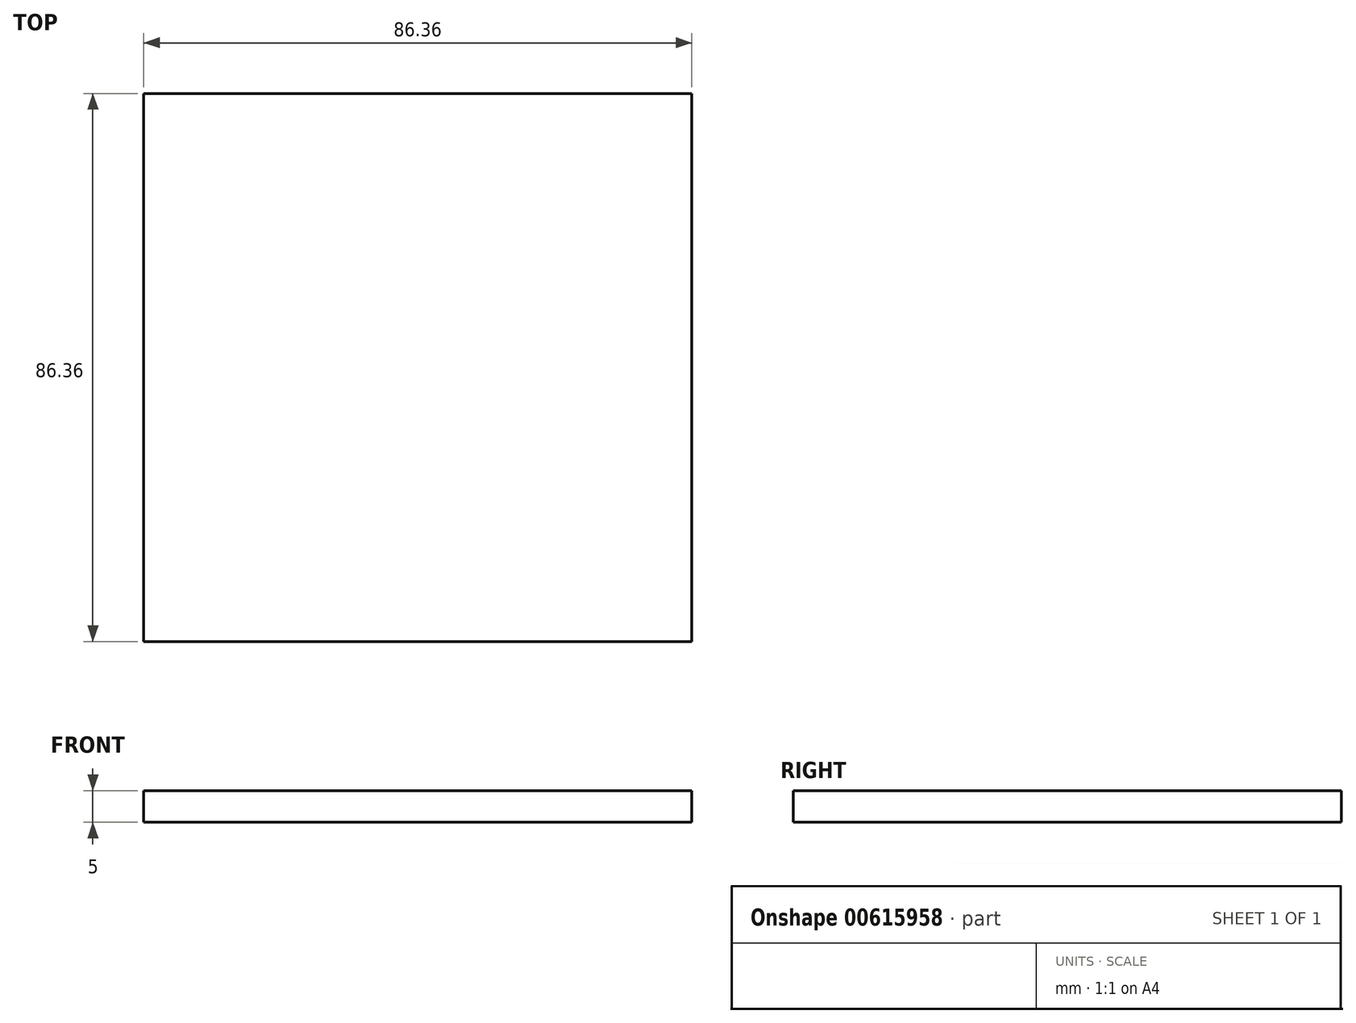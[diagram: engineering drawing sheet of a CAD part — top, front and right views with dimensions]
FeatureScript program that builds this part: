
annotation { "Feature Type Name" : "Feature", "Feature Type Description" : "" }
export const myFeature = defineFeature(function(context is Context, id is Id, definition is map)
    precondition{}
    {
        {
            var Q0;
            Q0=qCreatedBy(makeId("Top.planeOp"),FACE);
            var sketch = newSketch(context, id + "F0", { "sketchPlane" : qUnion([Q0])});
            skLineSegment(sketch, "E0.bottom", {"start": v(43.18, 43.18) * mm, "end": v(-43.18, 43.18) * mm});
            skLineSegment(sketch, "E0.top", {"start": v(43.18, -43.18) * mm, "end": v(-43.18, -43.18) * mm});
            skLineSegment(sketch, "E0.left", {"start": v(43.18, 43.18) * mm, "end": v(43.18, -43.18) * mm});
            skLineSegment(sketch, "E0.right", {"start": v(-43.18, 43.18) * mm, "end": v(-43.18, -43.18) * mm});
            skPoint(sketch, "E0.middle", {"position": v(0, 0) * mm});
            skSolve(sketch);
        }
        {
            var Q0;
            Q0=makeQuery(id+"F0.imprint","IMPRINT",FACE,{"disambiguationData":[TD([[makeQuery(id+"F0.imprint","IMPRINT",EDGE,{"derivedFrom":sQuery(id+"F0.wireOp",EDGE,"E0.bottom")}),1.0]])]});
            extrude(context, id + "F1", {"entities" : qUnion([Q0]), "depth" : 5 * mm, "offsetDistance" : 25.4 * mm});
        }
    });
